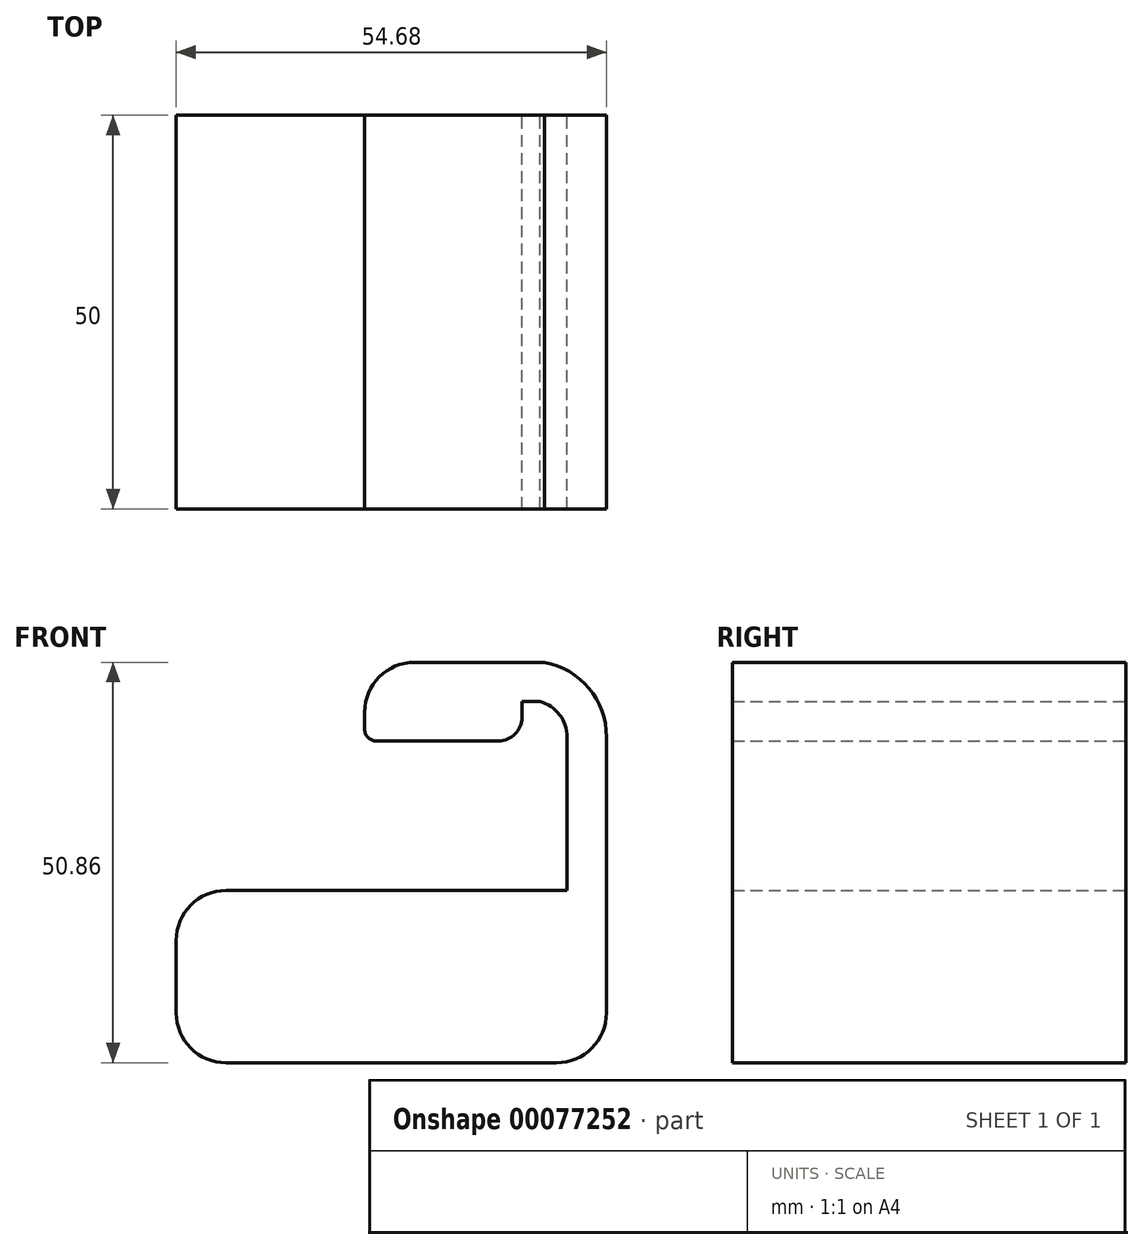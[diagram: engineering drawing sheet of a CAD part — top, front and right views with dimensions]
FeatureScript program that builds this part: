
annotation { "Feature Type Name" : "Feature", "Feature Type Description" : "" }
export const myFeature = defineFeature(function(context is Context, id is Id, definition is map)
    precondition{}
    {
        {
            var Q0;
            Q0=qCreatedBy(makeId("Front.planeOp"),FACE);
            var sketch = newSketch(context, id + "F0", { "sketchPlane" : qUnion([Q0])});
            skLineSegment(sketch, "E0.bottom", {"start": v(-20.99, 10.93) * mm, "end": v(27.34, 10.93) * mm});
            skLineSegment(sketch, "E0.top", {"start": v(-20.99, -10.93) * mm, "end": v(20.99, -10.93) * mm});
            skLineSegment(sketch, "E0.left", {"start": v(-27.34, 4.58) * mm, "end": v(-27.34, -4.58) * mm});
            skLineSegment(sketch, "E0.right", {"start": v(27.34, 10.93) * mm, "end": v(27.34, -4.58) * mm});
            skPoint(sketch, "E0.middle", {"position": v(0, 0) * mm});
            skLineSegment(sketch, "E1.bottom", {"start": v(2.96, 39.93) * mm, "end": v(16.61, 39.93) * mm});
            skLineSegment(sketch, "E1.top", {"start": v(-1.89, 29.93) * mm, "end": v(13.61, 29.93) * mm});
            skLineSegment(sketch, "E1.left", {"start": v(-3.39, 33.58) * mm, "end": v(-3.39, 31.43) * mm});
            skLineSegment(sketch, "E1.right", {"start": v(16.61, 39.93) * mm, "end": v(16.61, 32.93) * mm});
            skLineSegment(sketch, "E2", {"start": v(27.34, 10.93) * mm, "end": v(27.34, 30.43) * mm});
            skArc(sketch, "E3", {"start": v(27.34, 30.43) * mm, "mid": v(25.1, 36.6) * mm, "end": v(19.46, 39.93) * mm});
            skLineSegment(sketch, "E4", {"start": v(19.46, 39.93) * mm, "end": v(16.61, 39.93) * mm});
            skPoint(sketch, "E5.visualSharp", {"position": v(27.34, -10.93) * mm});
            skArc(sketch, "E5.filletArc", {"start": v(20.99, -10.93) * mm, "mid": v(25.48, -9.07) * mm, "end": v(27.34, -4.58) * mm});
            skPoint(sketch, "E6.visualSharp", {"position": v(-27.34, -10.93) * mm});
            skArc(sketch, "E6.filletArc", {"start": v(-27.34, -4.58) * mm, "mid": v(-25.48, -9.07) * mm, "end": v(-20.99, -10.93) * mm});
            skPoint(sketch, "E7.visualSharp", {"position": v(-27.34, 10.93) * mm});
            skArc(sketch, "E7.filletArc", {"start": v(-20.99, 10.93) * mm, "mid": v(-25.48, 9.07) * mm, "end": v(-27.34, 4.58) * mm});
            skPoint(sketch, "E8.visualSharp", {"position": v(-3.39, 39.93) * mm});
            skArc(sketch, "E8.filletArc", {"start": v(2.96, 39.93) * mm, "mid": v(-1.53, 38.07) * mm, "end": v(-3.39, 33.58) * mm});
            skLineSegment(sketch, "E9.0", {"start": v(18.9, 34.93) * mm, "end": v(16.61, 34.93) * mm});
            skArc(sketch, "E9.1", {"start": v(22.34, 30.43) * mm, "mid": v(21.38, 33.26) * mm, "end": v(18.9, 34.93) * mm});
            skLineSegment(sketch, "E9.2", {"start": v(22.34, 10.93) * mm, "end": v(22.34, 30.43) * mm});
            skPoint(sketch, "E10.visualSharp", {"position": v(16.61, 29.93) * mm});
            skArc(sketch, "E10.filletArc", {"start": v(13.61, 29.93) * mm, "mid": v(15.73, 30.8) * mm, "end": v(16.61, 32.93) * mm});
            skPoint(sketch, "E11.visualSharp", {"position": v(-3.39, 29.93) * mm});
            skArc(sketch, "E11.filletArc", {"start": v(-3.39, 31.43) * mm, "mid": v(-2.95, 30.37) * mm, "end": v(-1.89, 29.93) * mm});
            skSolve(sketch);
        }
        {
            var Q0;
            {var subQ1=sQuery(id+"F0.wireOp",EDGE,"E1.bottom");Q0=makeQuery(id+"F0.imprint","IMPRINT",FACE,{"disambiguationData":[TD([[makeQuery(id+"F0.imprint","IMPRINT",EDGE,{"derivedFrom":subQ1}),-1.0]])]});}
            var Q1;
            Q1=makeQuery(id+"F0.imprint","IMPRINT",FACE,{"disambiguationData":[TD([[makeQuery(id+"F0.imprint","IMPRINT",EDGE,{"derivedFrom":sQuery(id+"F0.wireOp",EDGE,"E0.top")}),1.0]])]});
            var Q2;
            {var subQ0=sQuery(id+"F0.wireOp",EDGE,"E2");Q2=makeQuery(id+"F0.imprint","IMPRINT",FACE,{"disambiguationData":[TD([[makeQuery(id+"F0.imprint","IMPRINT",EDGE,{"derivedFrom":subQ0}),1.0]])]});}
            extrude(context, id + "F1", {"entities" : qUnion([Q0, Q1, Q2]), "endBound" : BoundingType.SYMMETRIC, "depth" : 50 * mm});
        }
    });
